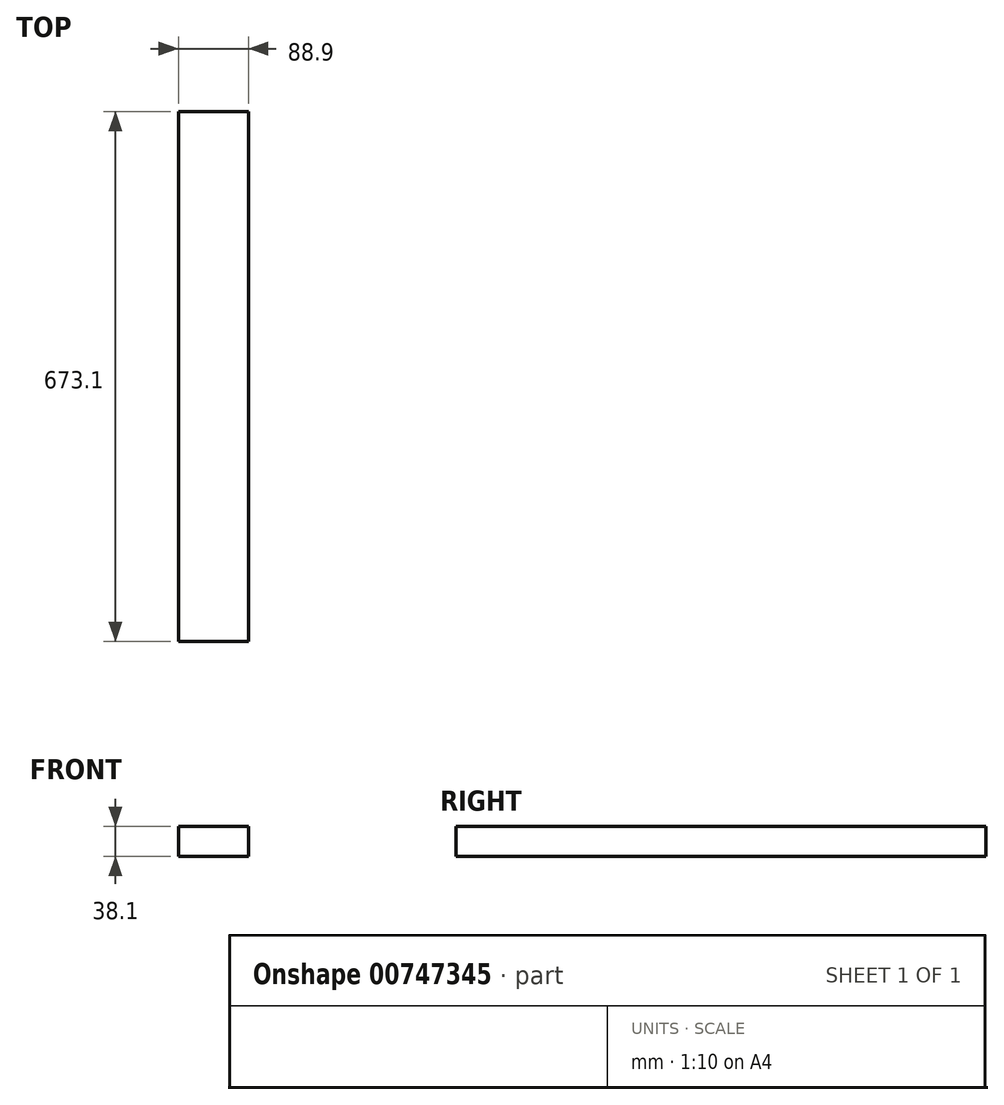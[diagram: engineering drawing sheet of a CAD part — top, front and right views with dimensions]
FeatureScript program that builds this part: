
annotation { "Feature Type Name" : "Feature", "Feature Type Description" : "" }
export const myFeature = defineFeature(function(context is Context, id is Id, definition is map)
    precondition{}
    {
        {
            var Q0;
            Q0=qCreatedBy(makeId("Front.planeOp"),FACE);
            var sketch = newSketch(context, id + "F0", { "sketchPlane" : qUnion([Q0])});
            skLineSegment(sketch, "E0.bottom", {"start": v(0, 0) * mm, "end": v(88.9, 0) * mm});
            skLineSegment(sketch, "E0.top", {"start": v(0, 38.1) * mm, "end": v(88.9, 38.1) * mm});
            skLineSegment(sketch, "E0.left", {"start": v(0, 0) * mm, "end": v(0, 38.1) * mm});
            skLineSegment(sketch, "E0.right", {"start": v(88.9, 0) * mm, "end": v(88.9, 38.1) * mm});
            skSolve(sketch);
        }
        {
            var Q0;
            Q0=qSketchRegion(id+"F0",true);
            extrude(context, id + "F1", {"entities" : qUnion([Q0]), "depth" : 673.1 * mm, "offsetDistance" : 25.4 * mm});
        }
    });
